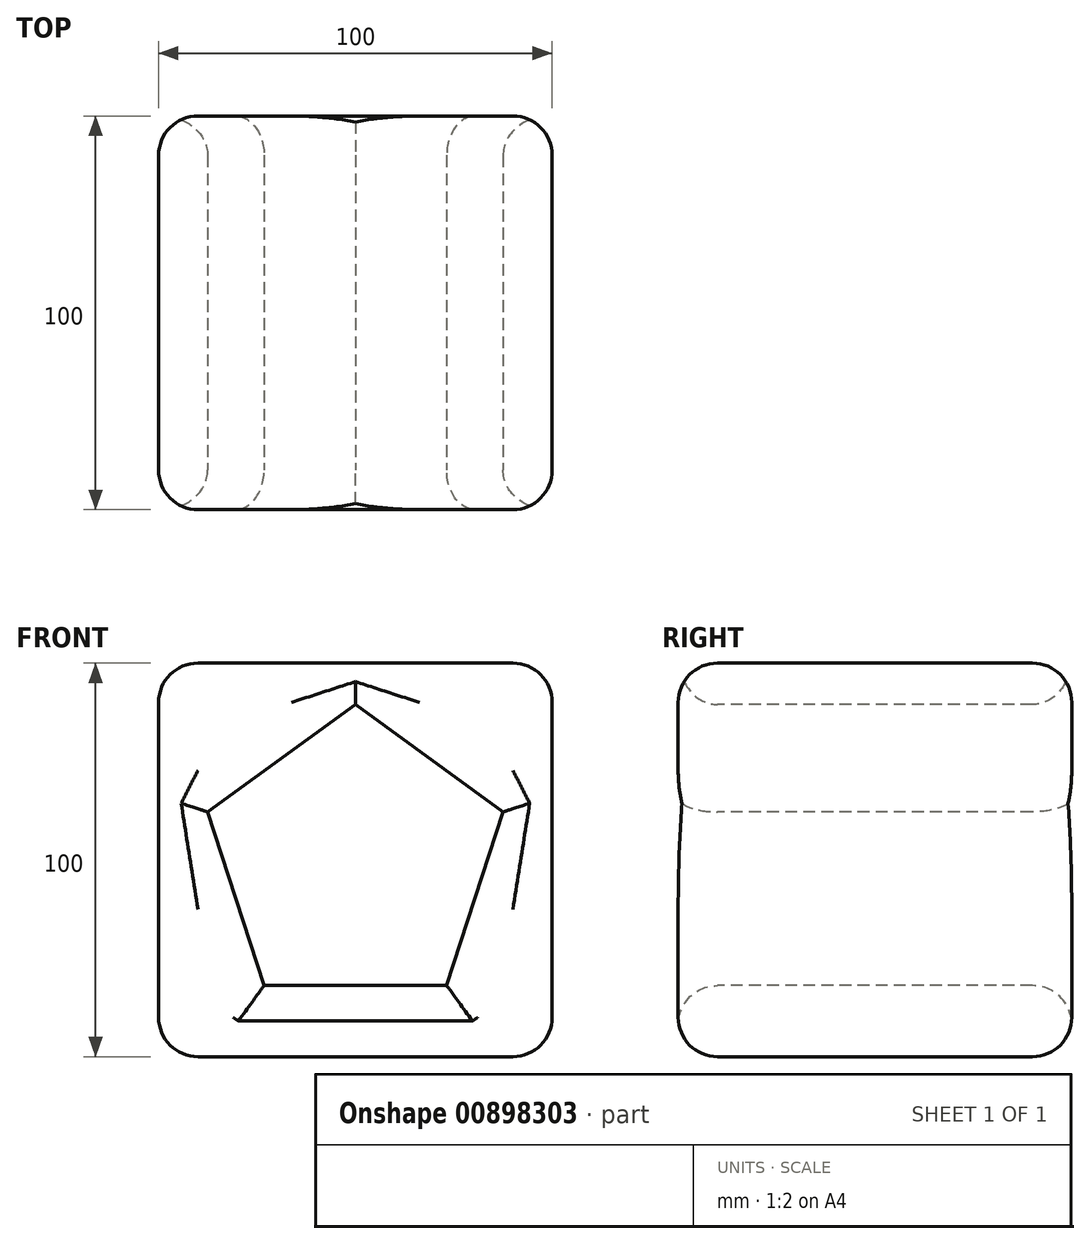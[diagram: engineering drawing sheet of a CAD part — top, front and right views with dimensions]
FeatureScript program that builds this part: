
annotation { "Feature Type Name" : "Feature", "Feature Type Description" : "" }
export const myFeature = defineFeature(function(context is Context, id is Id, definition is map)
    precondition{}
    {
        {
            var Q0;
            Q0=qCreatedBy(makeId("Front.planeOp"),FACE);
            var sketch = newSketch(context, id + "F0", { "sketchPlane" : qUnion([Q0])});
            skLineSegment(sketch, "E0.bottom", {"start": v(50, 50) * mm, "end": v(-50, 50) * mm});
            skLineSegment(sketch, "E0.top", {"start": v(50, -50) * mm, "end": v(-50, -50) * mm});
            skLineSegment(sketch, "E0.left", {"start": v(50, 50) * mm, "end": v(50, -50) * mm});
            skLineSegment(sketch, "E0.right", {"start": v(-50, 50) * mm, "end": v(-50, -50) * mm});
            skPoint(sketch, "E0.middle", {"position": v(0, 0) * mm});
            skSolve(sketch);
        }
        {
            var Q0;
            Q0=makeQuery(id+"F0.imprint","IMPRINT",FACE,{"disambiguationData":[TD([[makeQuery(id+"F0.imprint","IMPRINT",EDGE,{"derivedFrom":sQuery(id+"F0.wireOp",EDGE,"E0.bottom")}),1.0]])]});
            extrude(context, id + "F1", {"entities" : qUnion([Q0]), "depth" : 100 * mm, "offsetDistance" : 25 * mm});
        }
        {
            var Q0;
            Q0=makeQuery(id+"F1.opExtrude","CAP_FACE",FACE,{"disambiguationData":[OSD([sQuery(id+"F0.wireOp",EDGE,"E0.bottom"),sQuery(id+"F0.wireOp",EDGE,"E0.top"),sQuery(id+"F0.wireOp",EDGE,"E0.left"),sQuery(id+"F0.wireOp",EDGE,"E0.right")])],"isStart":false});
            var sketch = newSketch(context, id + "F2", { "sketchPlane" : qUnion([Q0])});
            skCircle(sketch, "E1.cCircle", {"center": v(0, 0) * mm, "radius": 39.45 * mm, "construction": true});
            skLineSegment(sketch, "E1.0", {"start": v(0, 39.45) * mm, "end": v(37.52, 12.2) * mm});
            skLineSegment(sketch, "E1.1", {"start": v(37.52, 12.2) * mm, "end": v(23.19, -31.92) * mm});
            skLineSegment(sketch, "E1.2", {"start": v(23.19, -31.92) * mm, "end": v(-23.19, -31.92) * mm});
            skLineSegment(sketch, "E1.3", {"start": v(-23.19, -31.92) * mm, "end": v(-37.52, 12.2) * mm});
            skLineSegment(sketch, "E1.4", {"start": v(-37.52, 12.2) * mm, "end": v(0, 39.45) * mm});
            skSolve(sketch);
        }
        {
            var Q0;
            Q0=makeQuery(id+"F2.imprint","IMPRINT",FACE,{"disambiguationData":[TD([[makeQuery(id+"F2.imprint","IMPRINT",EDGE,{"derivedFrom":sQuery(id+"F2.wireOp",EDGE,"E1.0")}),-1.0]])]});
            extrude(context, id + "F3", {"entities" : qUnion([Q0]), "operationType" : NewBodyOperationType.REMOVE, "oppositeDirection" : true, "depth" : 134.3 * mm, "offsetDistance" : 25 * mm});
        }
        {
            var Q0;
            Q0=makeQuery(id+"F1.opExtrude","SWEPT_FACE",FACE,{"disambiguationData":[OSD([sQuery(id+"F0.wireOp",EDGE,"E0.left")])]});
            var Q1;
            Q1=makeQuery(id+"F1.opExtrude","SWEPT_FACE",FACE,{"disambiguationData":[OSD([sQuery(id+"F0.wireOp",EDGE,"E0.bottom")])]});
            var Q2;
            Q2=makeQuery(id+"F1.opExtrude","SWEPT_FACE",FACE,{"disambiguationData":[OSD([sQuery(id+"F0.wireOp",EDGE,"E0.right")])]});
            var Q3;
            Q3=makeQuery(id+"F1.opExtrude","SWEPT_FACE",FACE,{"disambiguationData":[OSD([sQuery(id+"F0.wireOp",EDGE,"E0.top")])]});
            var Q4;
            Q4=makeQuery(id+"F1.opExtrude","CAP_FACE",FACE,{"disambiguationData":[OSD([sQuery(id+"F0.wireOp",EDGE,"E0.bottom"),sQuery(id+"F0.wireOp",EDGE,"E0.top"),sQuery(id+"F0.wireOp",EDGE,"E0.left"),sQuery(id+"F0.wireOp",EDGE,"E0.right")])],"isStart":true});
            var Q5;
            Q5=makeQuery(id+"F1.opExtrude","CAP_FACE",FACE,{"disambiguationData":[OSD([sQuery(id+"F0.wireOp",EDGE,"E0.bottom"),sQuery(id+"F0.wireOp",EDGE,"E0.top"),sQuery(id+"F0.wireOp",EDGE,"E0.left"),sQuery(id+"F0.wireOp",EDGE,"E0.right")])],"isStart":false});
            fillet(context, id + "F4", {"entities" : qUnion([Q0, Q1, Q2, Q3, Q4, Q5]), "radius" : 10 * mm, "tangentPropagation" : true, "allowEdgeOverflow" : false});
        }
    });
